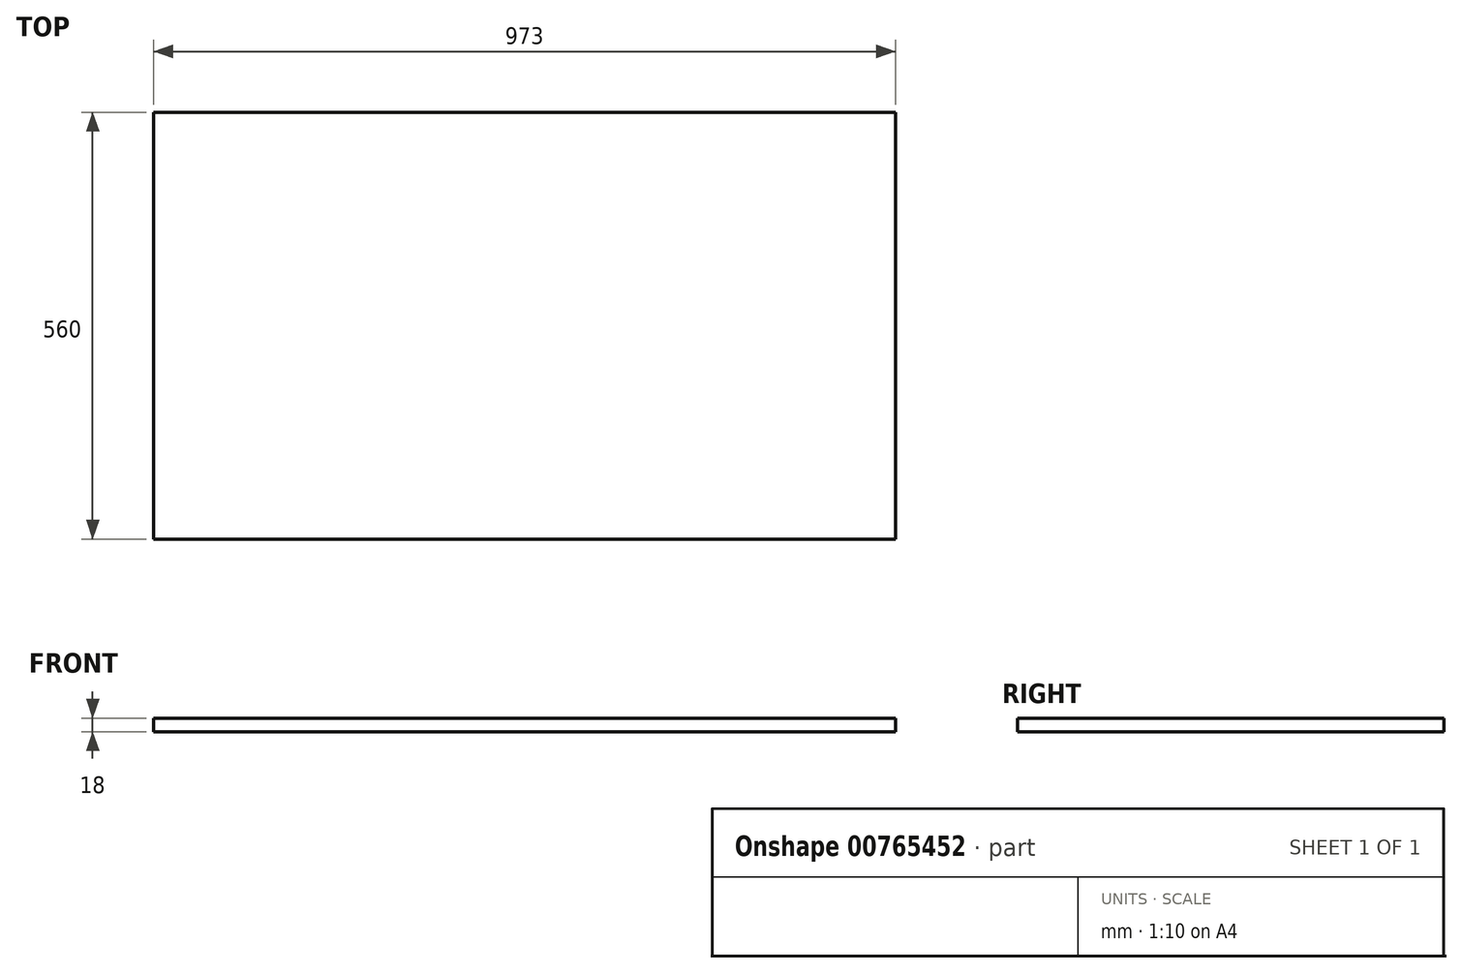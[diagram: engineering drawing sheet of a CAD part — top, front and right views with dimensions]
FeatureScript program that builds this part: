
annotation { "Feature Type Name" : "Feature", "Feature Type Description" : "" }
export const myFeature = defineFeature(function(context is Context, id is Id, definition is map)
    precondition{}
    {
        {
            var Q0;
            Q0=qCreatedBy(makeId("Top.planeOp"),FACE);
            var sketch = newSketch(context, id + "F0", { "sketchPlane" : qUnion([Q0])});
            skLineSegment(sketch, "E0.bottom", {"start": v(-486.5, -280) * mm, "end": v(486.5, -280) * mm});
            skLineSegment(sketch, "E0.top", {"start": v(-486.5, 280) * mm, "end": v(486.5, 280) * mm});
            skLineSegment(sketch, "E0.left", {"start": v(-486.5, -280) * mm, "end": v(-486.5, 280) * mm});
            skLineSegment(sketch, "E0.right", {"start": v(486.5, -280) * mm, "end": v(486.5, 280) * mm});
            skPoint(sketch, "E0.middle", {"position": v(0, 0) * mm});
            skSolve(sketch);
        }
        {
            var Q0;
            Q0 = qSketchRegion(id + "F0", true);
            extrude(context, id + "F1", {"entities" : qUnion([Q0]), "depth" : 18 * mm, "offsetDistance" : 25 * mm});
        }
    });
